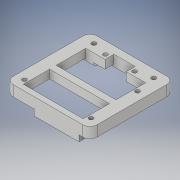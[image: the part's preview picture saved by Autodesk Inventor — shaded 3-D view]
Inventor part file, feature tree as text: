
AUTODESK INVENTOR PART (.ipt)
format: ipt  version: 2019 (Build 230136000, 136)  size: 214,016 bytes
history: native  units: in
note: dims shown in document units (in); Inventor stores cm internally (conversion verified against a paired STEP export)
features: extrude x5, sketch x5, fillet x1
ambient origin geometry x8: Origin, YZ Plane, XZ Plane, XY Plane, X Axis, Y Axis, Z Axis, Center Point
bodies: Solid1 (feature_tree)
feature tree (11):
  extrude  "Extrusion1"  Depth=0.3in TaperAngle=0.0deg
  extrude  "Extrusion2"  Depth=2.0in
  fillet  "Fillet1"  Radius=2.12in
  extrude  "Extrusion3"  Depth=0.2in
  extrude  "Extrusion4"  Depth=0.305in
  extrude  "Extrusion6"  Depth=0.2795in
  sketch  "Sketch1"  dims[d6=2.3622in d7=0.1181in d9=0.5413in d11=2.2114in d12=1.4764in d13=1.2894in d14=2.0176in d15=0.3386in d16=0.3in d17=0.0in]
  sketch  "Sketch2"  dims[d18=1.06in d19=2.0in d20=2.12in]
  sketch  "Sketch3"  dims[d21=0.0625in d22=0.0in d23=0.2in]
  sketch  "Sketch4"  dims[d24=0.787in d25=0.305in]
  sketch  "Sketch5"  dims[d26=0.169in d27=0.0in d42=0.441in d43=0.441in d44=0.191in d45=0.15in d46=0.191in d48=0.15in d49=0.25in d50=0.25in d51=0.0625in d52=0.0in d66=0.0803in d74=0.15in d75=0.0in d101=0.125in d102=0.2305in d104=0.2795in]
